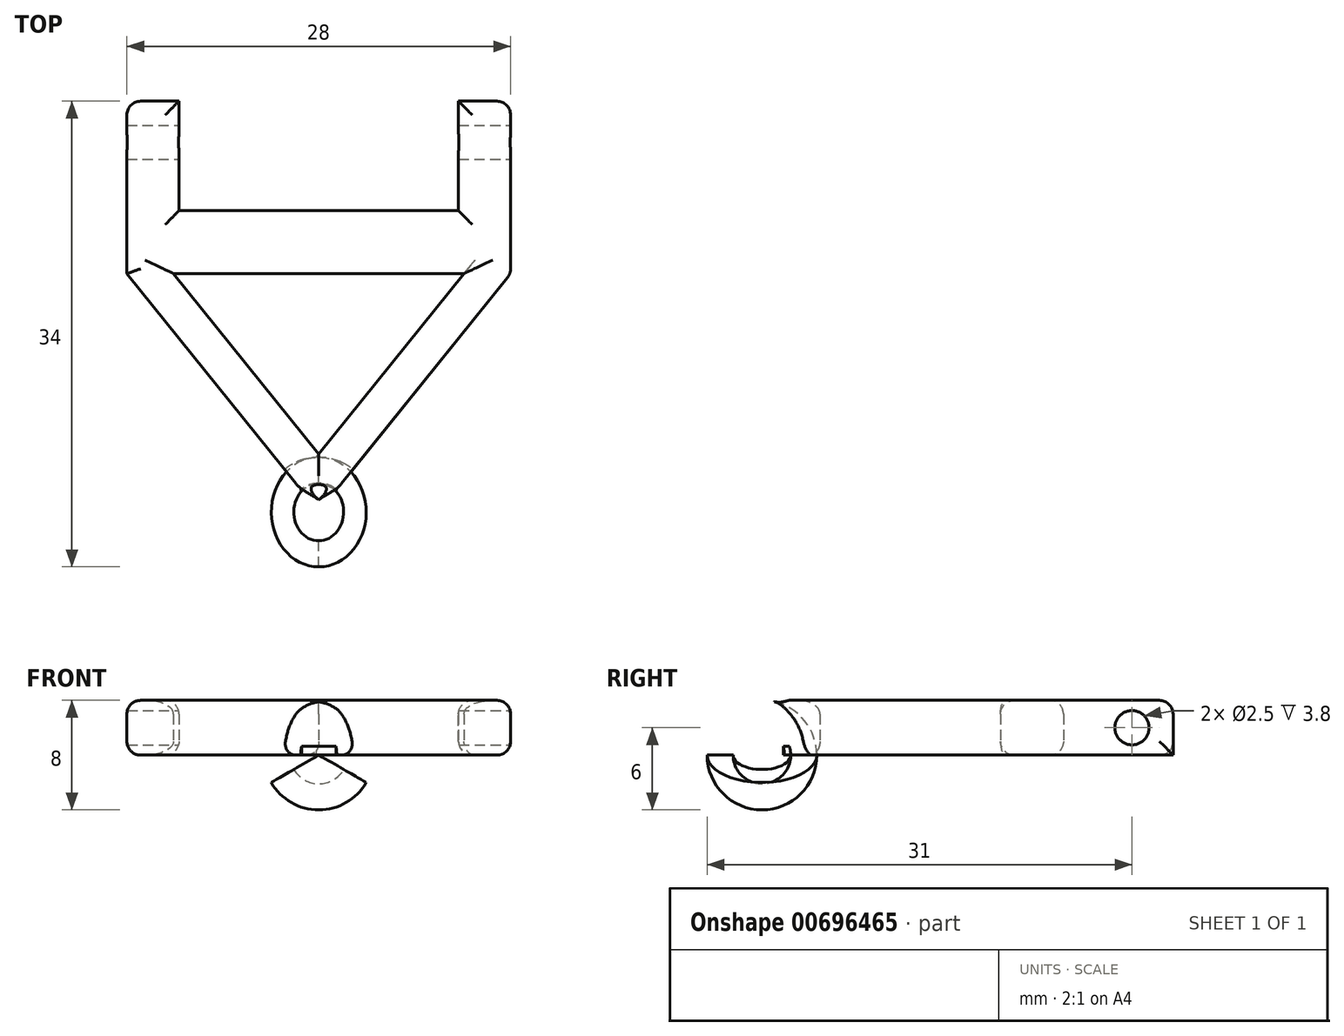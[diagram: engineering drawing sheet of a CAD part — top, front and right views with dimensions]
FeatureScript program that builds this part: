
annotation { "Feature Type Name" : "Feature", "Feature Type Description" : "" }
export const myFeature = defineFeature(function(context is Context, id is Id, definition is map)
    precondition{}
    {
        {
            var Q0;
            Q0=qCreatedBy(makeId("Top.planeOp"),FACE);
            var sketch = newSketch(context, id + "F0", { "sketchPlane" : qUnion([Q0])});
            skLineSegment(sketch, "E0.bottom", {"start": v(14, 15) * mm, "end": v(10.2, 15) * mm});
            skLineSegment(sketch, "E0.left", {"start": v(14, 15) * mm, "end": v(14, 2.4) * mm});
            skLineSegment(sketch, "E0.right", {"start": v(-14, 15) * mm, "end": v(-14, 2.4) * mm});
            skPoint(sketch, "E0.middle", {"position": v(0, 0) * mm});
            skLineSegment(sketch, "E1.top", {"start": v(10.2, 7) * mm, "end": v(-10.2, 7) * mm});
            skLineSegment(sketch, "E1.left", {"start": v(10.2, 15) * mm, "end": v(10.2, 7) * mm});
            skLineSegment(sketch, "E1.right", {"start": v(-10.2, 15) * mm, "end": v(-10.2, 7) * mm});
            skPoint(sketch, "E1.middle", {"position": v(0, 11) * mm});
            skLineSegment(sketch, "E2.trimOffspring", {"start": v(-10.2, 15) * mm, "end": v(-14, 15) * mm});
            skLineSegment(sketch, "E3", {"start": v(1.25, -13.44) * mm, "end": v(14, 2.4) * mm});
            skLineSegment(sketch, "E4", {"start": v(-14, 2.4) * mm, "end": v(-1.25, -13.44) * mm});
            skPoint(sketch, "E5.orphan", {"position": v(14, -15) * mm});
            skPoint(sketch, "E0.top.end.orphan", {"position": v(-14, -15) * mm});
            skLineSegment(sketch, "E6", {"start": v(0, -10.77) * mm, "end": v(10.6, 2.4) * mm});
            skLineSegment(sketch, "E7", {"start": v(10.6, 2.4) * mm, "end": v(-10.6, 2.4) * mm});
            skLineSegment(sketch, "E8", {"start": v(-10.6, 2.4) * mm, "end": v(0, -10.77) * mm});
            skArc(sketch, "E9", {"start": v(1.25, -13.44) * mm, "mid": v(0, -13) * mm, "end": v(-1.25, -13.44) * mm});
            skSolve(sketch);
        }
        {
            var Q0;
            Q0 = qSketchRegion(id + "F0", true);
            extrude(context, id + "F1", {"entities" : qUnion([Q0]), "depth" : 4 * mm, "offsetDistance" : 25 * mm});
        }
        {
            var Q0;
            Q0=makeQuery(id+"F1.opExtrude","CAP_FACE",FACE,{"disambiguationData":[OSD([sQuery(id+"F0.wireOp",EDGE,"E0.bottom"),sQuery(id+"F0.wireOp",EDGE,"E0.left"),sQuery(id+"F0.wireOp",EDGE,"E0.right"),sQuery(id+"F0.wireOp",EDGE,"E1.top"),sQuery(id+"F0.wireOp",EDGE,"E1.left"),sQuery(id+"F0.wireOp",EDGE,"E1.right"),sQuery(id+"F0.wireOp",EDGE,"E2.trimOffspring"),sQuery(id+"F0.wireOp",EDGE,"E3"),sQuery(id+"F0.wireOp",EDGE,"E4"),sQuery(id+"F0.wireOp",EDGE,"E6"),sQuery(id+"F0.wireOp",EDGE,"E7"),sQuery(id+"F0.wireOp",EDGE,"E8")])],"isStart":true});
            var sketch = newSketch(context, id + "F2", { "sketchPlane" : qUnion([Q0])});
            skArc(sketch, "E10", {"start": v(0, 11) * mm, "mid": v(4, 15) * mm, "end": v(0, 19) * mm});
            skArc(sketch, "E11", {"start": v(0, 12.9) * mm, "mid": v(2.1, 15) * mm, "end": v(0, 17.1) * mm});
            skLineSegment(sketch, "E12", {"start": v(0, 19) * mm, "end": v(0, 17.1) * mm});
            skLineSegment(sketch, "E13.trimOffspring", {"start": v(0, 12.9) * mm, "end": v(0, 11) * mm});
            skLineSegment(sketch, "E14", {"start": v(0, 0) * mm, "end": v(0, 24.4) * mm, "construction": true});
            skSolve(sketch);
        }
        {
            var Q0;
            Q0 = qSketchRegion(id + "F2", true);
            var Q1;
            Q1=sQuery(id+"F2.wireOp",EDGE,"E14");
            revolve(context, id + "F3", {"operationType" : NewBodyOperationType.ADD, "surfaceOperationType" : NewSurfaceOperationType.NEW, "entities" : qUnion([Q0]), "axis" : qUnion([Q1]), "revolveType" : RevolveType.TWO_DIRECTIONS, "angle" : 210 * degree, "angleBack" : 330 * degree});
        }
        {
            var Q0;
            Q0=makeQuery(id+"F1.opExtrude","CAP_EDGE",EDGE,{"disambiguationData":[OSD([sQuery(id+"F0.wireOp",EDGE,"E3")])],"isStart":false});
            var Q1;
            Q1=makeQuery(id+"F1.opExtrude","CAP_EDGE",EDGE,{"disambiguationData":[OSD([sQuery(id+"F0.wireOp",EDGE,"E4")])],"isStart":false});
            var Q2;
            Q2=makeQuery(id+"F1.opExtrude","CAP_EDGE",EDGE,{"disambiguationData":[OSD([sQuery(id+"F0.wireOp",EDGE,"E8")])],"isStart":false});
            var Q3;
            Q3=makeQuery(id+"F1.opExtrude","CAP_EDGE",EDGE,{"disambiguationData":[OSD([sQuery(id+"F0.wireOp",EDGE,"E6")])],"isStart":false});
            var Q4;
            {var subQ0=sQuery(id+"F0.wireOp",EDGE,"E3");var subQ2=sQuery(id+"F0.wireOp",EDGE,"E0.left");Q4=makeQuery(id+"F3.boolean.opBoolean","SPLIT",EDGE,{"disambiguationData":[TD([makeQuery(id+"F1.opExtrude","SWEPT_FACE",FACE,{"disambiguationData":[OSD([subQ2])]})])],"derivedFrom":makeQuery(id+"F1.opExtrude","CAP_EDGE",EDGE,{"disambiguationData":[OSD([subQ0])],"isStart":true})});}
            var Q5;
            Q5=makeQuery(id+"F1.opExtrude","SWEPT_EDGE",EDGE,{"disambiguationData":[OSD([sQuery(id+"F0.wireOp",EDGE,"E0.left"),sQuery(id+"F0.wireOp",EDGE,"E3")])]});
            var Q6;
            Q6=makeQuery(id+"F1.opExtrude","CAP_EDGE",EDGE,{"disambiguationData":[OSD([sQuery(id+"F0.wireOp",EDGE,"E7")])],"isStart":false});
            var Q7;
            Q7=makeQuery(id+"F1.opExtrude","CAP_EDGE",EDGE,{"disambiguationData":[OSD([sQuery(id+"F0.wireOp",EDGE,"E0.left")])],"isStart":false});
            var Q8;
            Q8=makeQuery(id+"F1.opExtrude","CAP_EDGE",EDGE,{"disambiguationData":[OSD([sQuery(id+"F0.wireOp",EDGE,"E0.left")])],"isStart":true});
            var Q9;
            Q9=makeQuery(id+"F1.opExtrude","CAP_EDGE",EDGE,{"disambiguationData":[OSD([sQuery(id+"F0.wireOp",EDGE,"E1.top")])],"isStart":false});
            var Q10;
            Q10=makeQuery(id+"F1.opExtrude","CAP_EDGE",EDGE,{"disambiguationData":[OSD([sQuery(id+"F0.wireOp",EDGE,"E1.right")])],"isStart":false});
            var Q11;
            Q11=makeQuery(id+"F1.opExtrude","CAP_EDGE",EDGE,{"disambiguationData":[OSD([sQuery(id+"F0.wireOp",EDGE,"E1.right")])],"isStart":true});
            var Q12;
            Q12=makeQuery(id+"F1.opExtrude","CAP_EDGE",EDGE,{"disambiguationData":[OSD([sQuery(id+"F0.wireOp",EDGE,"E1.left")])],"isStart":false});
            var Q13;
            Q13=makeQuery(id+"F1.opExtrude","CAP_EDGE",EDGE,{"disambiguationData":[OSD([sQuery(id+"F0.wireOp",EDGE,"E0.bottom")])],"isStart":false});
            var Q14;
            Q14=makeQuery(id+"F1.opExtrude","CAP_EDGE",EDGE,{"disambiguationData":[OSD([sQuery(id+"F0.wireOp",EDGE,"E8")])],"isStart":true});
            var Q15;
            {var subQ1=sQuery(id+"F0.wireOp",EDGE,"E4");var subQ2=sQuery(id+"F0.wireOp",EDGE,"E0.right");Q15=makeQuery(id+"F3.boolean.opBoolean","SPLIT",EDGE,{"disambiguationData":[TD([makeQuery(id+"F1.opExtrude","SWEPT_FACE",FACE,{"disambiguationData":[OSD([subQ2])]})])],"derivedFrom":makeQuery(id+"F1.opExtrude","CAP_EDGE",EDGE,{"disambiguationData":[OSD([subQ1])],"isStart":true})});}
            var Q16;
            Q16=makeQuery(id+"F1.opExtrude","CAP_EDGE",EDGE,{"disambiguationData":[OSD([sQuery(id+"F0.wireOp",EDGE,"E7")])],"isStart":true});
            var Q17;
            Q17=makeQuery(id+"F1.opExtrude","CAP_EDGE",EDGE,{"disambiguationData":[OSD([sQuery(id+"F0.wireOp",EDGE,"E1.top")])],"isStart":true});
            var Q18;
            Q18=makeQuery(id+"F1.opExtrude","CAP_EDGE",EDGE,{"disambiguationData":[OSD([sQuery(id+"F0.wireOp",EDGE,"E1.left")])],"isStart":true});
            var Q19;
            Q19=makeQuery(id+"F1.opExtrude","CAP_EDGE",EDGE,{"disambiguationData":[OSD([sQuery(id+"F0.wireOp",EDGE,"E0.right")])],"isStart":true});
            var Q20;
            Q20=makeQuery(id+"F1.opExtrude","SWEPT_EDGE",EDGE,{"disambiguationData":[OSD([sQuery(id+"F0.wireOp",EDGE,"E0.bottom"),sQuery(id+"F0.wireOp",EDGE,"E0.left")])]});
            var Q21;
            Q21=makeQuery(id+"F1.opExtrude","SWEPT_EDGE",EDGE,{"disambiguationData":[OSD([sQuery(id+"F0.wireOp",EDGE,"E0.right"),sQuery(id+"F0.wireOp",EDGE,"E2.trimOffspring")])]});
            var Q22;
            Q22=makeQuery(id+"F1.opExtrude","CAP_EDGE",EDGE,{"disambiguationData":[OSD([sQuery(id+"F0.wireOp",EDGE,"E2.trimOffspring")])],"isStart":false});
            var Q23;
            Q23=makeQuery(id+"F1.opExtrude","CAP_EDGE",EDGE,{"disambiguationData":[OSD([sQuery(id+"F0.wireOp",EDGE,"E2.trimOffspring")])],"isStart":true});
            var Q24;
            Q24=makeQuery(id+"F1.opExtrude","CAP_EDGE",EDGE,{"disambiguationData":[OSD([sQuery(id+"F0.wireOp",EDGE,"E0.right")])],"isStart":false});
            fillet(context, id + "F4", {"entities" : qUnion([Q0, Q1, Q2, Q3, Q4, Q5, Q6, Q7, Q8, Q9, Q10, Q11, Q12, Q13, Q14, Q15, Q16, Q17, Q18, Q19, Q20, Q21, Q22, Q23, Q24]), "radius" : 1 * mm, "tangentPropagation" : true, "allowEdgeOverflow" : false});
        }
        {
            var Q0;
            Q0=makeQuery(id+"F1.opExtrude","SWEPT_FACE",FACE,{"disambiguationData":[OSD([sQuery(id+"F0.wireOp",EDGE,"E0.left")])]});
            var sketch = newSketch(context, id + "F5", { "sketchPlane" : qUnion([Q0])});
            skCircle(sketch, "E15", {"center": v(12, 2) * mm, "radius": 1.25 * mm});
            skSolve(sketch);
        }
        {
            var Q0;
            Q0 = qSketchRegion(id + "F5", true);
            extrude(context, id + "F6", {"entities" : qUnion([Q0]), "operationType" : NewBodyOperationType.REMOVE, "endBound" : BoundingType.THROUGH_ALL, "oppositeDirection" : true, "depth" : 25 * mm, "offsetDistance" : 25 * mm});
        }
        {
            var Q0;
            Q0=makeQuery(id+"F3.boolean.opBoolean","INTERSECT",EDGE,{"derivedFrom":[makeQuery(id+"F1.opExtrude","SWEPT_FACE",FACE,{"disambiguationData":[OSD([sQuery(id+"F0.wireOp",EDGE,"E9")])]}),makeQuery(id+"F3.opRevolve","SWEPT_FACE",FACE,{"disambiguationData":[OSD([sQuery(id+"F2.wireOp",EDGE,"E10")])]})]});
            fillet(context, id + "F7", {"entities" : qUnion([Q0]), "radius" : 2 * mm, "tangentPropagation" : true, "allowEdgeOverflow" : false});
        }
    });
